# Revit family: Post_and_Wire_Bird_Deterrent_Nixalite
name_source: partatom
category: Specialty Equipment
revit_build: Autodesk Revit 2015 (Build: 20140223_1515(x64)
units: mm (PartAtom-declared; Revit-internal decimal feet)

## types (4) — shared parameters
Assembly Code = E1090900
Construction Details = http://www.arcat.com
Default Elevation = 0' - 0"
Green Building-LEED = http://www.arcat.com
Installation_Fabricaton = http://www.nixalite.com
Keynote = 10290
Manufacturer = Nixalite Architectural Bird Control
Manufacturer Fax = 888-624-1196
Manufacturer Website = http://www.nixalite.com
Post Finish = Metal - Stainless Steel
Product Data = http://www.arcat.com
Sales Information = http://www.nixalite.com
Send Message = http://www.arcat.com
Specification = http://arcat.com
Spring Finish = Metal - Black
URL = http://www.nixalite.com
Wire Finish = Metal - Stainless Steel
zero-valued in all types: Expected Lifespan (Years), Maintenance Schedule (Months), Warranty Duration (Years)

## per-type parameters (varying)
| type | Base Visible | Cover | Description | Height | Mid Wire Height | Model | Recess Into Host |
| Nail Point Tall | No | Yes | Nixalite Post and Wire Deterrent System - Nail Point Tall as Specified | 0' - 5" | 0' - 2 7/32" | Nail Point 6" | 0' - 1" |
| Nail Point Short | No | Yes | Nixalite Post and Wire Deterrent System - Nail Point Short as Specified | 0' - 3 1/2" | 0' - 1 15/32" | Nail Point 4.5" | 0' - 1" |
| Flite Base Tall | Yes | No | Nixalite Post and Wire Deterrent System - Flite Base Tall as Specified | 0' - 5" | 0' - 2 7/32" | Flite Base 5" | 0' - 0" |
| Flite Base Short | Yes | No | Nixalite Post and Wire Deterrent System - Flite Base Short as Specified | 0' - 3 1/2" | 0' - 1 15/32" | Flite Base 3.5" | 0' - 0" |

## geometry (parser evidence)
native form markers: Blend x4, Sweep x5
no freeform markers — native parametric forms only
